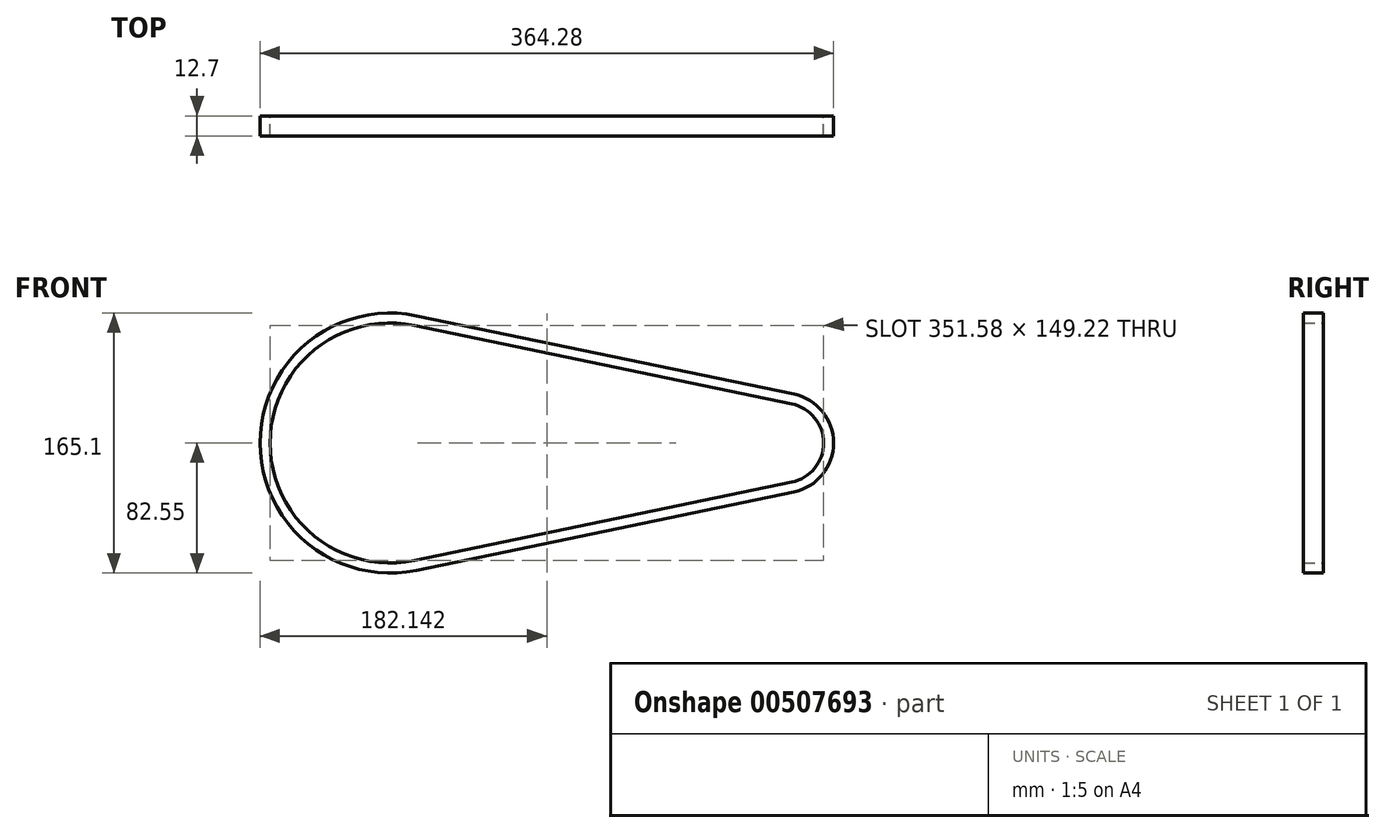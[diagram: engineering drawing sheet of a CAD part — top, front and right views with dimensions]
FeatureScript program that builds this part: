
annotation { "Feature Type Name" : "Feature", "Feature Type Description" : "" }
export const myFeature = defineFeature(function(context is Context, id is Id, definition is map)
    precondition{}
    {
        {
            var Q0;
            Q0=qCreatedBy(makeId("Front.planeOp"),FACE);
            var sketch = newSketch(context, id + "F0", { "sketchPlane" : qUnion([Q0])});
            skArc(sketch, "E0", {"start": v(15.48, 74.61) * mm, "mid": v(-76.2, 0) * mm, "end": v(15.48, -74.61) * mm});
            skLineSegment(sketch, "E1", {"start": v(0, 0) * mm, "end": v(249.98, 0) * mm, "construction": true});
            skArc(sketch, "E2", {"start": v(255.15, -24.87) * mm, "mid": v(275.38, 0) * mm, "end": v(255.15, 24.87) * mm});
            skLineSegment(sketch, "E3", {"start": v(15.48, 74.61) * mm, "end": v(255.15, 24.87) * mm});
            skLineSegment(sketch, "E4.MirrorCS", {"start": v(15.48, -74.61) * mm, "end": v(255.15, -24.87) * mm});
            skArc(sketch, "E5.0", {"start": v(16.78, 80.83) * mm, "mid": v(-82.55, 0) * mm, "end": v(16.78, -80.83) * mm});
            skLineSegment(sketch, "E5.1", {"start": v(16.78, 80.83) * mm, "end": v(256.44, 31.09) * mm});
            skArc(sketch, "E5.2", {"start": v(256.44, -31.09) * mm, "mid": v(281.73, 0) * mm, "end": v(256.44, 31.09) * mm});
            skLineSegment(sketch, "E5.3", {"start": v(16.78, -80.83) * mm, "end": v(256.44, -31.09) * mm});
            skSolve(sketch);
        }
        {
            var Q0;
            Q0 = qSketchRegion(id + "F0", true);
            extrude(context, id + "F1", {"entities" : qUnion([Q0]), "depth" : 12.7 * mm, "offsetDistance" : 25.4 * mm});
        }
    });
